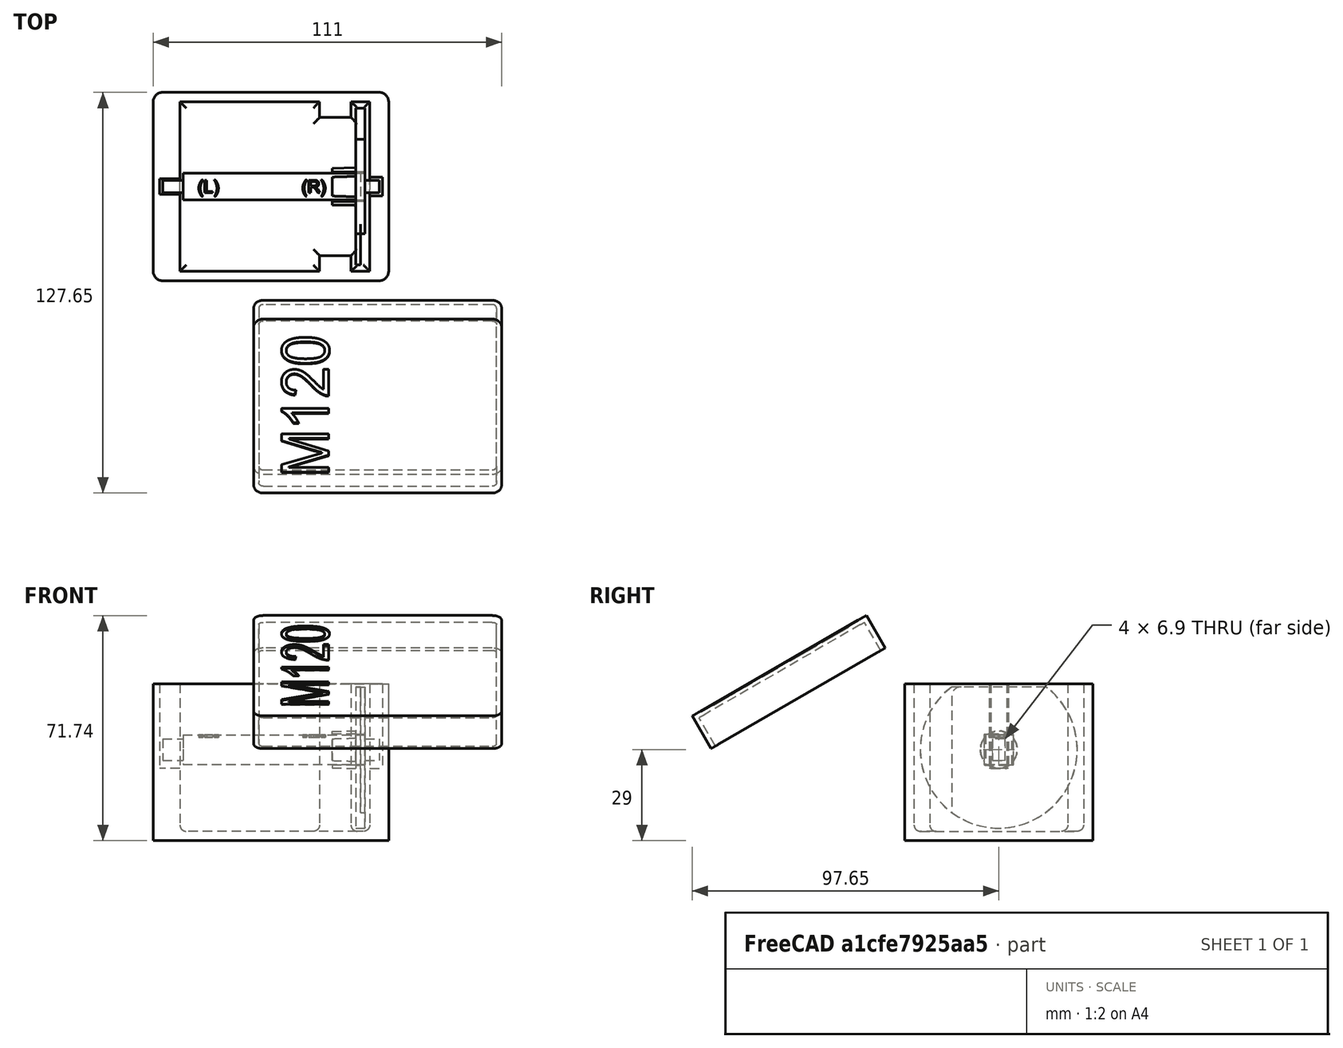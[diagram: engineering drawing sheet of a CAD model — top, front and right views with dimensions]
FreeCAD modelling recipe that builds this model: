
FCSTD DOCUMENT  (FreeCAD 1.0R39109 (Git))
Label: Phomeno_M120_Rolle
License: All rights reserved
LicenseURL: https://en.wikipedia.org/wiki/All_rights_reserved
objects: TechDraw::DrawViewDimension×24, Sketcher::SketchObject×13, PartDesign::Pad×7, PartDesign::Pocket×6, TechDraw::DrawProjGroupItem×6, PartDesign::Body×5, Part::Part2DObjectPython×2, PartDesign::Fillet×2, TechDraw::DrawSVGTemplate×2, TechDraw::DrawProjGroup×2, TechDraw::DrawPage×2, PartDesign::FeatureBase×1, PartDesign::Plane×1, PartDesign::Mirrored×1, PartDesign::Thickness×1, Part::Fuse×1
note: 124 computed .brp shape members not serialized (recipe doc carries the construction recipe); baked Part::Feature solids carry a one-line shape summary decoded from their .brp

FEATURE [Sketcher::SketchObject] Sketch  label="s_Basis_Platte_links"
  ArcFitTolerance = 1e-06
  AttachmentSupport = -> [YZ_Plane]
  FullyConstrained = true
  MakeInternals = false
  MapMode = 5
  Placement = pos=(0,0,0) rot=(0.57735,0.57735,0.57735;2.0944rad)
  sketch-geometry (3):
    g0: Circle [constr] CenterX=0 CenterY=0 CenterZ=0 NormalX=0 NormalY=0 NormalZ=1 AngleXU=0 Radius=25
    g1: LineSegment StartX=-15 StartY=20 StartZ=0 EndX=15 EndY=20 EndZ=0
    g2: ArcOfCircle CenterX=0 CenterY=0 CenterZ=0 NormalX=0 NormalY=0 NormalZ=1 AngleXU=0 Radius=25 StartAngle=2.2143 EndAngle=7.21048
  constraints (8):
    c: Coincident(g0,g-1)
    c: Diameter(g0) = 50
    c: PointOnObject(g1,g0)
    c: Horizontal(g1)
    c: Coincident(g2,g1)
    c: Coincident(g2,g0)
    c: Coincident(g2,g1)
    c: Distance(g-1,g1) = 20
FEATURE [PartDesign::Pad] Pad  label="Basis_Platte_links"
  Direction = (1,0,0)
  Length = 1.5
  Length2 = 10
  Placement = pos=(0,0,0) rot=(1,1,1;2.0944rad)
  Profile = -> Sketch
  ReferenceAxis = -> Sketch [N_Axis]
  Refine = true
  Suppressed = false
  Type = 0
FEATURE [Sketcher::SketchObject] Sketch001  label="s_Achsenloch_links"
  ArcFitTolerance = 1e-06
  AttachmentSupport = -> [YZ_Plane]
  FullyConstrained = true
  MakeInternals = false
  MapMode = 5
  Placement = pos=(0,0,0) rot=(0.57735,0.57735,0.57735;2.0944rad)
  sketch-geometry (4):
    g0: LineSegment StartX=-4.5 StartY=5 StartZ=0 EndX=-4.5 EndY=-5 EndZ=0
    g1: LineSegment StartX=-4.5 StartY=-5 StartZ=0 EndX=4.5 EndY=-5 EndZ=0
    g2: LineSegment StartX=4.5 StartY=-5 StartZ=0 EndX=4.5 EndY=5 EndZ=0
    g3: LineSegment StartX=4.5 StartY=5 StartZ=0 EndX=-4.5 EndY=5 EndZ=0
  constraints (11):
    c: Coincident(g0,g1)
    c: Coincident(g1,g2)
    c: Coincident(g2,g3)
    c: Coincident(g3,g0)
    c: Vertical(g0)
    c: Vertical(g2)
    c: Horizontal(g1)
    c: Horizontal(g3)
    c: Distance(g3,g3) = 9
    c: Symmetric(g2,g0,g-1)
    c: Distance(g2,g2) = 10
FEATURE [Sketcher::SketchObject] Sketch002  label="s_Achse_links"
  ArcFitTolerance = 1e-06
  AttachmentSupport = -> [YZ_Plane]
  FullyConstrained = true
  MakeInternals = false
  MapMode = 5
  Placement = pos=(0,0,0) rot=(0.57735,0.57735,0.57735;2.0944rad)
  sketch-geometry (1):
    g0: Circle CenterX=0 CenterY=0 CenterZ=0 NormalX=0 NormalY=0 NormalZ=1 AngleXU=0 Radius=6
  constraints (2):
    c: Coincident(g0,g-1)
    c: Diameter(g0) = 12
FEATURE [PartDesign::Pad] Pad001  label="Achse_links"
  BaseFeature = -> Pad
  Direction = (1,0,0)
  Length = 9
  Length2 = 10
  Placement = pos=(0,0,0) rot=(1,1,1;2.0944rad)
  Profile = -> Sketch002
  ReferenceAxis = -> Sketch002 [N_Axis]
  Refine = true
  Suppressed = false
  TaperAngle = -1
  Type = 0
FEATURE [PartDesign::Pocket] Pocket  label="Achsenloch_links"
  BaseFeature = -> Pad001
  Direction = (-1,0,0)
  Length = 10
  Length2 = 10
  Midplane = true
  Placement = pos=(0,0,0) rot=(1,1,1;2.0944rad)
  Profile = -> Sketch001
  ReferenceAxis = -> Sketch001 [N_Axis]
  Refine = true
  Suppressed = false
  Type = 1
FEATURE [Sketcher::SketchObject] Sketch003  label="s_Aussparung_Achse_links"
  ArcFitTolerance = 1e-06
  AttachmentSupport = -> [YZ_Plane]
  ExternalGeometry = -> [Sketch001]
  FullyConstrained = true
  MakeInternals = false
  MapMode = 5
  Placement = pos=(0,0,0) rot=(0.57735,0.57735,0.57735;2.0944rad)
  sketch-geometry (4):
    g0: LineSegment StartX=-4.7 StartY=4.8 StartZ=0 EndX=-4.7 EndY=-4.8 EndZ=0
    g1: LineSegment StartX=-4.7 StartY=-4.8 StartZ=0 EndX=4.7 EndY=-4.8 EndZ=0
    g2: LineSegment StartX=4.7 StartY=-4.8 StartZ=0 EndX=4.7 EndY=4.8 EndZ=0
    g3: LineSegment StartX=4.7 StartY=4.8 StartZ=0 EndX=-4.7 EndY=4.8 EndZ=0
  constraints (11):
    c: Coincident(g0,g1)
    c: Coincident(g1,g2)
    c: Coincident(g2,g3)
    c: Coincident(g3,g0)
    c: Vertical(g0)
    c: Vertical(g2)
    c: Horizontal(g1)
    c: Horizontal(g3)
    c: Symmetric(g2,g0,g-1)
    c: Distance(g-3,g3) = 0.2
    c: DistanceX(g-4,g2) = 0.2
FEATURE [PartDesign::Pocket] Pocket001  label="Aussparung_Achse_links"
  BaseFeature = -> Pocket
  Direction = (-1,0,0)
  Length = 5
  Length2 = 5
  Placement = pos=(0,0,0) rot=(1,1,1;2.0944rad)
  Profile = -> Sketch003
  ReferenceAxis = -> Sketch003 [N_Axis]
  Refine = true
  Reversed = true
  Suppressed = false
  Type = 1
FEATURE [PartDesign::Body] Body  label="Platte_Links"
  AllowCompound = false
  Group = -> [Sketch,Pad,Sketch001,Sketch002,Pad001,Pocket,Sketch003,Pocket001]
  Origin = -> Origin
  Placement = pos=(-14,0,0) rot=(0,0,1;0rad)
  Tip = -> Pocket001
FEATURE [Sketcher::SketchObject] Sketch004  label="s_Achse_aussen"
  ArcFitTolerance = 1e-06
  AttachmentSupport = -> [YZ_Plane001]
  FullyConstrained = true
  MakeInternals = false
  MapMode = 5
  Placement = pos=(0,0,0) rot=(0.57735,0.57735,0.57735;2.0944rad)
  sketch-geometry (4):
    g0: LineSegment StartX=-4.25 StartY=4.75 StartZ=0 EndX=-4.25 EndY=-4.75 EndZ=0
    g1: LineSegment StartX=-4.25 StartY=-4.75 StartZ=0 EndX=4.25 EndY=-4.75 EndZ=0
    g2: LineSegment StartX=4.25 StartY=-4.75 StartZ=0 EndX=4.25 EndY=4.75 EndZ=0
    g3: LineSegment StartX=4.25 StartY=4.75 StartZ=0 EndX=-4.25 EndY=4.75 EndZ=0
  constraints (11):
    c: Coincident(g0,g1)
    c: Coincident(g1,g2)
    c: Coincident(g2,g3)
    c: Coincident(g3,g0)
    c: Vertical(g0)
    c: Vertical(g2)
    c: Horizontal(g1)
    c: Horizontal(g3)
    c: Symmetric(g2,g0,g-1)
    c: Distance(g1,g1) = 8.5
    c: Distance(g2,g2) = 9.5
FEATURE [Sketcher::SketchObject] Sketch005  label="s_Achse_innen"
  ArcFitTolerance = 1e-06
  AttachmentSupport = -> [YZ_Plane001]
  FullyConstrained = true
  MakeInternals = false
  MapMode = 5
  Placement = pos=(0,0,0) rot=(0.57735,0.57735,0.57735;2.0944rad)
  sketch-geometry (4):
    g0: LineSegment StartX=-2 StartY=3.45 StartZ=0 EndX=-2 EndY=-3.45 EndZ=0
    g1: LineSegment StartX=-2 StartY=-3.45 StartZ=0 EndX=2 EndY=-3.45 EndZ=0
    g2: LineSegment StartX=2 StartY=-3.45 StartZ=0 EndX=2 EndY=3.45 EndZ=0
    g3: LineSegment StartX=2 StartY=3.45 StartZ=0 EndX=-2 EndY=3.45 EndZ=0
  constraints (11):
    c: Coincident(g0,g1)
    c: Coincident(g1,g2)
    c: Coincident(g2,g3)
    c: Coincident(g3,g0)
    c: Vertical(g0)
    c: Vertical(g2)
    c: Horizontal(g1)
    c: Horizontal(g3)
    c: Symmetric(g2,g0,g-1)
    c: Distance(g3,g3) = 4
    c: DistanceY(g2,g2) = 6.9
FEATURE [PartDesign::Pad] Pad002  label="Achse_innen"
  Direction = (1,0,0)
  Length = 69
  Length2 = 10
  Midplane = true
  Placement = pos=(0,0,0) rot=(1,1,1;2.0944rad)
  Profile = -> Sketch005
  ReferenceAxis = -> Sketch005 [N_Axis]
  Refine = true
  Suppressed = false
  Type = 0
FEATURE [PartDesign::Pad] Pad003  label="Achse_aussen"
  BaseFeature = -> Pad002
  Direction = (1,0,0)
  Length = 30
  Length2 = 28
  Midplane = true
  Placement = pos=(0,0,0) rot=(1,1,1;2.0944rad)
  Profile = -> Sketch004
  ReferenceAxis = -> Sketch004 [N_Axis]
  Refine = true
  Suppressed = false
  Type = 4
FEATURE [PartDesign::FeatureBase] Clone  label="Clone_Platte_Links"
  BaseFeature = -> Body
  Placement = pos=(-49,0,0) rot=(0,0,1;0rad)
  Suppressed = false
FEATURE [Sketcher::SketchObject] Sketch006  label="s_Auftrag"
  ArcFitTolerance = 1e-06
  AttachmentSupport = -> [Clone]
  ExternalGeometry = -> [Clone]
  FullyConstrained = true
  MakeInternals = false
  MapMode = 5
  Placement = pos=(-49,0,0) rot=(0.57735,-0.57735,-0.57735;2.0944rad)
  sketch-geometry (9):
    g0: LineSegment StartX=15 StartY=20 StartZ=0 EndX=-12 EndY=20 EndZ=0
    g1: LineSegment StartX=-15 StartY=17 StartZ=0 EndX=-15 EndY=-20 EndZ=0
    g2: ArcOfCircle CenterX=0 CenterY=0 CenterZ=0 NormalX=0 NormalY=0 NormalZ=1 AngleXU=0 Radius=25 StartAngle=4.06889 EndAngle=7.21048
    g3: LineSegment StartX=-4.7 StartY=4.8 StartZ=0 EndX=-4.7 EndY=-4.8 EndZ=0
    g4: LineSegment StartX=-4.7 StartY=-4.8 StartZ=0 EndX=4.7 EndY=-4.8 EndZ=0
    g5: LineSegment StartX=4.7 StartY=-4.8 StartZ=0 EndX=4.7 EndY=4.8 EndZ=0
    g6: LineSegment StartX=4.7 StartY=4.8 StartZ=0 EndX=-4.7 EndY=4.8 EndZ=0
    g7: ArcOfCircle CenterX=-12 CenterY=17 CenterZ=0 NormalX=0 NormalY=0 NormalZ=1 AngleXU=0 Radius=3 StartAngle=1.5708 EndAngle=3.14159
    g8: GeomPoint [constr] X=-15 Y=20 Z=0
  constraints (21):
    c: Coincident(g0,g-4)
    c: Coincident(g8,g-4)
    c: Coincident(g2,g0)
    c: Coincident(g2,g1)
    c: Coincident(g2,g-1)
    c: Coincident(g3,g4)
    c: Coincident(g4,g5)
    c: Coincident(g5,g6)
    c: Coincident(g6,g3)
    c: Vertical(g3)
    c: Vertical(g5)
    c: Horizontal(g4)
    c: Horizontal(g6)
    c: Coincident(g3,g-6)
    c: Coincident(g4,g-8)
    c: Vertical(g1)
    c: PointOnObject(g8,g0)
    c: PointOnObject(g8,g1)
    c: Tangent(g0,g7) = -1.5708
    c: Tangent(g1,g7) = -1.5708
    c: Radius(g7) = 3
FEATURE [PartDesign::Pad] Pad004  label="Auftrag"
  BaseFeature = -> Clone
  Direction = (-1,0,0)
  Length = 1.5
  Length2 = 10
  Placement = pos=(-49,0,0) rot=(0,0,1;0rad)
  Profile = -> Sketch006
  ReferenceAxis = -> Sketch006 [N_Axis]
  Refine = true
  Suppressed = false
  Type = 0
FEATURE [PartDesign::Body] Body003  label="Platte_Rechts"
  AllowCompound = false
  Group = -> [Clone,Sketch006,Pad004]
  Origin = -> Origin003
  Placement = pos=(-20.5,1.54e-14,0) rot=(0,0,1;3.14159rad)
  Tip = -> Pad004
FEATURE [Part::Part2DObjectPython] ShapeString  label="ss_Beschriftung"  # Draft 2D object (typed FeaturePython)
  FontFile = <path>
  Fuse = false
  Justification = 6
  JustificationReference = 0
  KeepLeftMargin = false
  MakeFace = true
  ObliqueAngle = 0
  Placement = pos=(-23,-2,5) rot=(0,0,1;0rad)
  ScaleToSize = true
  Size = 4
  String = (L)                 (R)
  Tracking = 0
FEATURE [Sketcher::SketchObject] Sketch008  label="s_Box-Body"
  ArcFitTolerance = 1e-06
  AttachmentSupport = -> [XY_Plane004]
  FullyConstrained = true
  MakeInternals = false
  MapMode = 5
  sketch-geometry (4):
    g0: LineSegment StartX=-37.5 StartY=30 StartZ=0 EndX=-37.5 EndY=-30 EndZ=0
    g1: LineSegment StartX=-37.5 StartY=-30 StartZ=0 EndX=37.5 EndY=-30 EndZ=0
    g2: LineSegment StartX=37.5 StartY=-30 StartZ=0 EndX=37.5 EndY=30 EndZ=0
    g3: LineSegment StartX=37.5 StartY=30 StartZ=0 EndX=-37.5 EndY=30 EndZ=0
  constraints (11):
    c: Coincident(g0,g1)
    c: Coincident(g1,g2)
    c: Coincident(g2,g3)
    c: Coincident(g3,g0)
    c: Vertical(g0)
    c: Vertical(g2)
    c: Horizontal(g1)
    c: Horizontal(g3)
    c: Symmetric(g2,g0,g-1)
    c: DistanceX(g1,g1) = 75
    c: DistanceY(g2,g2) = 60
FEATURE [PartDesign::Pad] Pad005  label="Box-Body"
  Direction = (0,0,1)
  Length = 21
  Length2 = 29
  Midplane = true
  Profile = -> Sketch008
  ReferenceAxis = -> Sketch008 [N_Axis]
  Refine = true
  Suppressed = false
  Type = 4
FEATURE [PartDesign::Plane] DatumPlane  label="dp_top"
  AttachmentSupport = -> [Pad005]
  Length = 88.4164
  MapMode = 5
  Placement = pos=(0,0,21) rot=(0,0,1;0rad)
  ResizeMode = 0
  Width = 73.4164
FEATURE [Sketcher::SketchObject] Sketch009  label="s_Box-Innen"
  ArcFitTolerance = 1e-06
  AttachmentSupport = -> [DatumPlane]
  ExternalGeometry = -> [Sketch008]
  FullyConstrained = true
  MakeInternals = false
  MapMode = 5
  Placement = pos=(0,0,21) rot=(0,0,1;0rad)
  sketch-geometry (8):
    g0: LineSegment StartX=31.5 StartY=0 StartZ=0 EndX=31.5 EndY=27 EndZ=0
    g1: LineSegment StartX=31.5 StartY=27 StartZ=0 EndX=25.5 EndY=27 EndZ=0
    g2: LineSegment StartX=25.5 StartY=27 StartZ=0 EndX=25.5 EndY=22 EndZ=0
    g3: LineSegment StartX=-29 StartY=27 StartZ=0 EndX=-29 EndY=0 EndZ=0
    g4: LineSegment StartX=25.5 StartY=22 StartZ=0 EndX=15.5 EndY=22 EndZ=0
    g5: LineSegment StartX=15.5 StartY=22 StartZ=0 EndX=15.5 EndY=27 EndZ=0
    g6: LineSegment StartX=15.5 StartY=27 StartZ=0 EndX=-29 EndY=27 EndZ=0
    g7: LineSegment StartX=-29 StartY=0 StartZ=0 EndX=31.5 EndY=0 EndZ=0
  constraints (24):
    c: Vertical(g0)
    c: Coincident(g0,g1)
    c: Horizontal(g1)
    c: Coincident(g1,g2)
    c: Vertical(g2)
    c: PointOnObject(g0,g-1)
    c: PointOnObject(g3,g-1)
    c: Vertical(g3)
    c: Coincident(g2,g4)
    c: Horizontal(g4)
    c: Coincident(g4,g5)
    c: Vertical(g5)
    c: Coincident(g5,g6)
    c: Horizontal(g6)
    c: Coincident(g3,g6)
    c: DistanceY(g2,g2) = 5
    c: DistanceX(g0,g-4) = 6
    c: DistanceY(g0,g-4) = 3
    c: DistanceX(g1,g1) = 6
    c: DistanceX(g4,g4) = 10
    c: DistanceX(g-5,g3) = 8.5
    c: Equal(g2,g5)
    c: Coincident(g7,g3)
    c: Coincident(g7,g0)
FEATURE [PartDesign::Pocket] Pocket003  label="Box-Innen_halb"
  BaseFeature = -> Pad005
  Direction = (0,0,-1)
  Length = 47
  Length2 = 5
  Profile = -> Sketch009
  ReferenceAxis = -> Sketch009 [N_Axis]
  Refine = true
  Suppressed = false
  Type = 0
FEATURE [PartDesign::Mirrored] Mirrored  label="Box-Innen"
  BaseFeature = -> Pocket003
  MirrorPlane = -> Sketch009 [H_Axis]
  Originals = -> [Pocket003]
  Refine = true
  Suppressed = false
  TransformMode = 0
FEATURE [Sketcher::SketchObject] Sketch010  label="s_Fuehrung_Achse"
  ArcFitTolerance = 1e-06
  AttachmentSupport = -> [DatumPlane]
  ExternalGeometry = -> [Sketch009]
  FullyConstrained = true
  MakeInternals = false
  MapMode = 5
  Placement = pos=(0,0,21) rot=(0,0,1;0rad)
  sketch-geometry (8):
    g0: LineSegment StartX=31.5 StartY=3 StartZ=0 EndX=31.5 EndY=-3 EndZ=0
    g1: LineSegment StartX=31.5 StartY=-3 StartZ=0 EndX=35.5 EndY=-3 EndZ=0
    g2: LineSegment StartX=35.5 StartY=-3 StartZ=0 EndX=35.5 EndY=3 EndZ=0
    g3: LineSegment StartX=35.5 StartY=3 StartZ=0 EndX=31.5 EndY=3 EndZ=0
    g4: LineSegment StartX=-29 StartY=2.5 StartZ=0 EndX=-35.5 EndY=2.5 EndZ=0
    g5: LineSegment StartX=-35.5 StartY=2.5 StartZ=0 EndX=-35.5 EndY=-2.5 EndZ=0
    g6: LineSegment StartX=-35.5 StartY=-2.5 StartZ=0 EndX=-29 EndY=-2.5 EndZ=0
    g7: LineSegment StartX=-29 StartY=-2.5 StartZ=0 EndX=-29 EndY=2.5 EndZ=0
  constraints (22):
    c: Coincident(g0,g1)
    c: Coincident(g1,g2)
    c: Coincident(g2,g3)
    c: Coincident(g3,g0)
    c: Vertical(g0)
    c: Horizontal(g1)
    c: Horizontal(g3)
    c: PointOnObject(g0,g-3)
    c: Symmetric(g2,g1,g-1)
    c: Distance(g3,g3) = 4
    c: DistanceY(g-1,g2) = 3
    c: Coincident(g4,g5)
    c: Coincident(g5,g6)
    c: Coincident(g6,g7)
    c: Coincident(g7,g4)
    c: Horizontal(g4)
    c: Horizontal(g6)
    c: Vertical(g7)
    c: PointOnObject(g4,g-4)
    c: Symmetric(g4,g5,g-1)
    c: DistanceX(g4,g4) = 6.5
    c: DistanceY(g5,g-1) = 2.5
FEATURE [PartDesign::Pocket] Pocket004  label="Fuerhrung_Achse"
  BaseFeature = -> Mirrored
  Direction = (0,0,-1)
  Length = 27
  Length2 = 5
  Profile = -> Sketch010
  ReferenceAxis = -> Sketch010 [N_Axis]
  Refine = true
  Suppressed = false
  Type = 0
FEATURE [PartDesign::Fillet] Fillet  label="Abrundung_Aussenkanten"
  Base = -> Pocket004 [Edge1,Edge5,Edge8,Edge2]
  BaseFeature = -> Pocket004
  Radius = 3
  Refine = true
  SupportTransform = false
  Suppressed = false
  UseAllEdges = false
FEATURE [PartDesign::Fillet] Fillet001  label="Abrundung_innen"
  Base = -> Fillet [Edge77,Edge79,Edge81,Edge83,Edge84,Edge49,Edge57,Edge59,Edge61,Edge63,Edge65,Edge66]
  BaseFeature = -> Fillet
  Radius = 2
  Refine = true
  SupportTransform = false
  Suppressed = false
  UseAllEdges = false
FEATURE [PartDesign::Body] Body004  label="Spool-Box-Body"
  AllowCompound = false
  Group = -> [Sketch008,Pad005,DatumPlane,Sketch009,Pocket003,Mirrored,Sketch010,Pocket004,Fillet,Fillet001]
  Origin = -> Origin004
  Tip = -> Fillet001
FEATURE [Sketcher::SketchObject] Sketch011  label="s_Deckel_Body"
  ArcFitTolerance = 1e-06
  AttachmentSupport = -> [XY_Plane005]
  FullyConstrained = true
  MakeInternals = false
  MapMode = 5
  sketch-geometry (12):
    g0: LineSegment StartX=-39.5 StartY=29 StartZ=0 EndX=-39.5 EndY=-29 EndZ=0
    g1: LineSegment StartX=-36.5 StartY=-32 StartZ=0 EndX=36.5 EndY=-32 EndZ=0
    g2: LineSegment StartX=39.5 StartY=-29 StartZ=0 EndX=39.5 EndY=29 EndZ=0
    g3: LineSegment StartX=36.5 StartY=32 StartZ=0 EndX=-36.5 EndY=32 EndZ=0
    g4: ArcOfCircle CenterX=-36.5 CenterY=29 CenterZ=0 NormalX=0 NormalY=0 NormalZ=1 AngleXU=0 Radius=3 StartAngle=1.5708 EndAngle=3.14159
    g5: GeomPoint [constr] X=-39.5 Y=32 Z=0
    g6: ArcOfCircle CenterX=36.5 CenterY=29 CenterZ=0 NormalX=0 NormalY=0 NormalZ=1 AngleXU=0 Radius=3 StartAngle=4e-16 EndAngle=1.5708
    g7: GeomPoint [constr] X=39.5 Y=32 Z=0
    g8: ArcOfCircle CenterX=36.5 CenterY=-29 CenterZ=0 NormalX=0 NormalY=0 NormalZ=1 AngleXU=0 Radius=3 StartAngle=4.71239 EndAngle=6.28319
    g9: GeomPoint [constr] X=39.5 Y=-32 Z=0
    g10: ArcOfCircle CenterX=-36.5 CenterY=-29 CenterZ=0 NormalX=0 NormalY=0 NormalZ=1 AngleXU=0 Radius=3 StartAngle=3.14159 EndAngle=4.71239
    g11: GeomPoint [constr] X=-39.5 Y=-32 Z=0
  constraints (27):
    c: Vertical(g0)
    c: Vertical(g2)
    c: Horizontal(g1)
    c: Horizontal(g3)
    c: Symmetric(g7,g11,g-1)
    c: DistanceX(g5,g7) = 79
    c: DistanceY(g9,g7) = 64
    c: PointOnObject(g5,g0)
    c: PointOnObject(g5,g3)
    c: Tangent(g0,g4) = -1.5708
    c: Tangent(g3,g4) = -1.5708
    c: PointOnObject(g7,g2)
    c: PointOnObject(g7,g3)
    c: Tangent(g2,g6) = -1.5708
    c: Tangent(g3,g6) = -1.5708
    c: PointOnObject(g9,g1)
    c: PointOnObject(g9,g2)
    c: Tangent(g1,g8) = -1.5708
    c: Tangent(g2,g8) = -1.5708
    c: PointOnObject(g11,g0)
    c: PointOnObject(g11,g1)
    c: Tangent(g0,g10) = -1.5708
    c: Tangent(g1,g10) = -1.5708
    c: Radius(g4) = 3
    c: Equal(g4,g6)
    c: Equal(g6,g8)
    c: Equal(g8,g10)
FEATURE [PartDesign::Pad] Pad006  label="Deckel_Body"
  Direction = (0,0,1)
  Length = 12
  Length2 = 10
  Profile = -> Sketch011
  ReferenceAxis = -> Sketch011 [N_Axis]
  Refine = true
  Suppressed = false
  Type = 0
FEATURE [PartDesign::Thickness] Thickness  label="Deckelform"
  Base = -> Pad006 [Face9]
  BaseFeature = -> Pad006
  Intersection = false
  Join = 0
  Mode = 0
  Refine = true
  Reversed = true
  SupportTransform = false
  Suppressed = false
  Value = 1.6
FEATURE [Part::Part2DObjectPython] ShapeString001  label="ss_Schrift_Deckel"  # Draft 2D object (typed FeaturePython)
  FontFile = <path>
  Fuse = false
  Justification = 6
  JustificationReference = 0
  KeepLeftMargin = false
  MakeFace = true
  ObliqueAngle = 0
  Placement = pos=(-31.53,-9.43,0) rot=(0,0,1;0rad)
  ScaleToSize = true
  Size = 15
  String = M120
  Tracking = 0
FEATURE [Sketcher::SketchObject] Sketch012  label="s_Schrift_Deckel"
  ArcFitTolerance = 1e-06
  AttachmentOffset = pos=(-25,7,0) rot=(0,0,1;1.5708rad)
  AttachmentSupport = -> [Thickness]
  FullyConstrained = false
  MakeInternals = false
  MapMode = 5
  Placement = pos=(-25,7,12) rot=(0,0,1;1.5708rad)
  sketch-geometry (66):
    g0: LineSegment StartX=-31.53 StartY=-9.43 StartZ=0 EndX=-31.53 EndY=5.57 EndZ=0
    g1: LineSegment StartX=-29.6189 StartY=-9.43 StartZ=0 EndX=-31.53 EndY=-9.43 EndZ=0
    g2: LineSegment StartX=-29.6189 StartY=3.34207 StartZ=0 EndX=-29.6189 EndY=-9.43 EndZ=0
    g3: LineSegment StartX=-25.2857 StartY=-9.43 StartZ=0 EndX=-29.6189 EndY=3.34207 EndZ=0
    g4: LineSegment StartX=-23.4972 StartY=-9.43 StartZ=0 EndX=-25.2857 EndY=-9.43 EndZ=0
    g5: LineSegment StartX=-19.1436 StartY=3.12746 StartZ=0 EndX=-23.4972 EndY=-9.43 EndZ=0
    g6: LineSegment StartX=-19.1436 StartY=-9.43 StartZ=0 EndX=-19.1436 EndY=3.12746 EndZ=0
    g7: LineSegment StartX=-17.2324 StartY=-9.43 StartZ=0 EndX=-19.1436 EndY=-9.43 EndZ=0
    g8: LineSegment StartX=-17.2324 StartY=5.57 StartZ=0 EndX=-17.2324 EndY=-9.43 EndZ=0
    g9: LineSegment StartX=-19.8998 StartY=5.57 StartZ=0 EndX=-17.2324 EndY=5.57 EndZ=0
    g10: LineSegment StartX=-23.487 StartY=-4.86854 StartZ=0 EndX=-19.8998 EndY=5.57 EndZ=0
    g11: BSplineCurve PolesCount=3 KnotsCount=2 Degree=2 IsPeriodic=0
    g12: BSplineCurve PolesCount=3 KnotsCount=2 Degree=2 IsPeriodic=0
    g13: LineSegment StartX=-28.5458 StartY=5.57 StartZ=0 EndX=-24.9995 EndY=-5.05318 EndZ=0
    g14: LineSegment StartX=-31.53 StartY=5.57 StartZ=0 EndX=-28.5458 EndY=5.57 EndZ=0
    g15: LineSegment StartX=-7.84382 StartY=-9.43 StartZ=0 EndX=-9.68339 EndY=-9.43 EndZ=0
    g16: LineSegment StartX=-7.84382 StartY=5.65721 StartZ=0 EndX=-7.84382 EndY=-9.43 EndZ=0
    g17: LineSegment StartX=-9.02932 StartY=5.65721 StartZ=0 EndX=-7.84382 EndY=5.65721 EndZ=0
    g18: BSplineCurve PolesCount=3 KnotsCount=2 Degree=2 IsPeriodic=0
    g19: BSplineCurve PolesCount=3 KnotsCount=2 Degree=2 IsPeriodic=0
    g20: LineSegment StartX=-13.3625 StartY=0.119419 StartZ=0 EndX=-13.3625 EndY=1.90721 EndZ=0
    g21: BSplineCurve PolesCount=3 KnotsCount=2 Degree=2 IsPeriodic=0
    g22: BSplineCurve PolesCount=3 KnotsCount=2 Degree=2 IsPeriodic=0
    g23: LineSegment StartX=-9.68339 StartY=-9.43 StartZ=0 EndX=-9.68339 EndY=2.32622 EndZ=0
    g24: LineSegment StartX=6.53754 StartY=-7.69672 StartZ=0 EndX=6.53754 EndY=-9.43 EndZ=0
    g25: LineSegment StartX=-0.810523 StartY=-7.69672 StartZ=0 EndX=6.53754 EndY=-7.69672 EndZ=0
    g26: BSplineCurve PolesCount=3 KnotsCount=2 Degree=2 IsPeriodic=0
    g27: BSplineCurve PolesCount=3 KnotsCount=2 Degree=2 IsPeriodic=0
    g28: BSplineCurve PolesCount=3 KnotsCount=2 Degree=2 IsPeriodic=0
    g29: BSplineCurve PolesCount=3 KnotsCount=2 Degree=2 IsPeriodic=0
    g30: BSplineCurve PolesCount=3 KnotsCount=2 Degree=2 IsPeriodic=0
    g31: BSplineCurve PolesCount=3 KnotsCount=2 Degree=2 IsPeriodic=0
    g32: BSplineCurve PolesCount=3 KnotsCount=2 Degree=2 IsPeriodic=0
    g33: BSplineCurve PolesCount=3 KnotsCount=2 Degree=2 IsPeriodic=0
    g34: BSplineCurve PolesCount=3 KnotsCount=2 Degree=2 IsPeriodic=0
    g35: LineSegment StartX=-1.12734 StartY=1.07872 StartZ=0 EndX=-3.01801 EndY=1.27494 EndZ=0
    g36: BSplineCurve PolesCount=3 KnotsCount=2 Degree=2 IsPeriodic=0
    g37: BSplineCurve PolesCount=3 KnotsCount=2 Degree=2 IsPeriodic=0
    g38: BSplineCurve PolesCount=3 KnotsCount=2 Degree=2 IsPeriodic=0
    g39: BSplineCurve PolesCount=3 KnotsCount=2 Degree=2 IsPeriodic=0
    g40: BSplineCurve PolesCount=3 KnotsCount=2 Degree=2 IsPeriodic=0
    g41: BSplineCurve PolesCount=3 KnotsCount=2 Degree=2 IsPeriodic=0
    g42: BSplineCurve PolesCount=3 KnotsCount=2 Degree=2 IsPeriodic=0
    g43: BSplineCurve PolesCount=3 KnotsCount=2 Degree=2 IsPeriodic=0
    g44: BSplineCurve PolesCount=3 KnotsCount=2 Degree=2 IsPeriodic=0
    g45: LineSegment StartX=6.53754 StartY=-9.43 StartZ=0 EndX=-3.36548 EndY=-9.43 EndZ=0
    g46: BSplineCurve PolesCount=3 KnotsCount=2 Degree=2 IsPeriodic=0
    g47: BSplineCurve PolesCount=3 KnotsCount=2 Degree=2 IsPeriodic=0
    g48: BSplineCurve PolesCount=3 KnotsCount=2 Degree=2 IsPeriodic=0
    g49: BSplineCurve PolesCount=3 KnotsCount=2 Degree=2 IsPeriodic=0
    g50: BSplineCurve PolesCount=3 KnotsCount=2 Degree=2 IsPeriodic=0
    g51: BSplineCurve PolesCount=3 KnotsCount=2 Degree=2 IsPeriodic=0
    g52: BSplineCurve PolesCount=3 KnotsCount=2 Degree=2 IsPeriodic=0
    g53: BSplineCurve PolesCount=3 KnotsCount=2 Degree=2 IsPeriodic=0
    g54: BSplineCurve PolesCount=3 KnotsCount=2 Degree=2 IsPeriodic=0
    g55: BSplineCurve PolesCount=3 KnotsCount=2 Degree=2 IsPeriodic=0
    g56: BSplineCurve PolesCount=3 KnotsCount=2 Degree=2 IsPeriodic=0
    g57: BSplineCurve PolesCount=3 KnotsCount=2 Degree=2 IsPeriodic=0
    g58: BSplineCurve PolesCount=3 KnotsCount=2 Degree=2 IsPeriodic=0
    g59: BSplineCurve PolesCount=3 KnotsCount=2 Degree=2 IsPeriodic=0
    g60: BSplineCurve PolesCount=3 KnotsCount=2 Degree=2 IsPeriodic=0
    g61: BSplineCurve PolesCount=3 KnotsCount=2 Degree=2 IsPeriodic=0
    g62: BSplineCurve PolesCount=3 KnotsCount=2 Degree=2 IsPeriodic=0
    g63: BSplineCurve PolesCount=3 KnotsCount=2 Degree=2 IsPeriodic=0
    g64: BSplineCurve PolesCount=3 KnotsCount=2 Degree=2 IsPeriodic=0
    g65: BSplineCurve PolesCount=3 KnotsCount=2 Degree=2 IsPeriodic=0
  constraints (83):
    c: Vertical(g0)
    c: Coincident(g0,g1)
    c: Horizontal(g1)
    c: Coincident(g1,g2)
    c: Vertical(g2)
    c: Coincident(g2,g3)
    c: Coincident(g3,g4)
    c: Horizontal(g4)
    c: Coincident(g4,g5)
    c: Coincident(g5,g6)
    c: Vertical(g6)
    c: Coincident(g6,g7)
    c: Horizontal(g7)
    c: Coincident(g7,g8)
    c: Vertical(g8)
    c: Coincident(g8,g9)
    c: Horizontal(g9)
    c: Coincident(g9,g10)
    c: Coincident(g10,g11)
    c: Coincident(g11,g12)
    c: Coincident(g12,g13)
    c: Coincident(g13,g14)
    c: Horizontal(g14)
    c: Coincident(g14,g0)
    c: Horizontal(g15)
    c: Coincident(g15,g16)
    c: Vertical(g16)
    c: Coincident(g16,g17)
    c: Horizontal(g17)
    c: Coincident(g17,g18)
    c: Coincident(g18,g19)
    c: Coincident(g19,g20)
    c: Vertical(g20)
    c: Coincident(g20,g21)
    c: Coincident(g21,g22)
    c: Coincident(g22,g23)
    c: Vertical(g23)
    c: Coincident(g23,g15)
    c: Vertical(g24)
    c: Coincident(g24,g25)
    c: Horizontal(g25)
    c: Coincident(g25,g26)
    c: Coincident(g26,g27)
    c: Coincident(g27,g28)
    c: Coincident(g28,g29)
    c: Coincident(g29,g30)
    c: Coincident(g30,g31)
    c: Coincident(g31,g32)
    c: Coincident(g32,g33)
    c: Coincident(g33,g34)
    c: Coincident(g34,g35)
    c: Coincident(g35,g36)
    c: Coincident(g36,g37)
    c: Coincident(g37,g38)
    c: Coincident(g38,g39)
    c: Coincident(g39,g40)
    c: Coincident(g40,g41)
    c: Coincident(g41,g42)
    c: Coincident(g42,g43)
    c: Coincident(g43,g44)
    c: Coincident(g44,g45)
    c: Horizontal(g45)
    c: Coincident(g45,g24)
    c: Coincident(g46,g47)
    c: Coincident(g47,g48)
    c: Coincident(g48,g49)
    c: Coincident(g49,g50)
    c: Coincident(g50,g51)
    c: Coincident(g51,g52)
    c: Coincident(g52,g53)
    c: Coincident(g53,g54)
    c: Coincident(g54,g55)
    c: Coincident(g55,g56)
    c: Coincident(g56,g57)
    c: Coincident(g57,g46)
    c: Coincident(g58,g59)
    c: Coincident(g59,g60)
    c: Coincident(g60,g61)
    c: Coincident(g61,g62)
    c: Coincident(g62,g63)
    c: Coincident(g63,g64)
    c: Coincident(g64,g65)
    c: Coincident(g65,g58)
FEATURE [PartDesign::Pocket] Pocket005  label="SchriftDeckel"
  BaseFeature = -> Thickness
  Direction = (0,0,-1)
  Length = 0.4
  Length2 = 5
  Profile = -> Sketch012
  ReferenceAxis = -> Sketch012 [N_Axis]
  Refine = true
  Suppressed = false
  Type = 0
FEATURE [PartDesign::Body] Body005  label="Spool-Box-Deckel"
  AllowCompound = false
  Group = -> [Sketch011,Pad006,Thickness,ShapeString001,Sketch012,Pocket005]
  Origin = -> Origin005
  Placement = pos=(34,-63.9379,16.3507) rot=(1,0,0;0.523599rad)
  Tip = -> Pocket005
FEATURE [Sketcher::SketchObject] Sketch013  label="s_Beschriftung"
  ArcFitTolerance = 1e-06
  FullyConstrained = false
  MakeInternals = false
  Placement = pos=(0,0,5) rot=(0,0,1;0rad)
  sketch-geometry (73):
    g0: BSplineCurve PolesCount=3 KnotsCount=2 Degree=2 IsPeriodic=0
    g1: LineSegment StartX=-21.681 StartY=-3.16279 StartZ=0 EndX=-22.0325 EndY=-3.16279 EndZ=0
    g2: BSplineCurve PolesCount=3 KnotsCount=2 Degree=2 IsPeriodic=0
    g3: BSplineCurve PolesCount=3 KnotsCount=2 Degree=2 IsPeriodic=0
    g4: BSplineCurve PolesCount=3 KnotsCount=2 Degree=2 IsPeriodic=0
    g5: BSplineCurve PolesCount=3 KnotsCount=2 Degree=2 IsPeriodic=0
    g6: LineSegment StartX=-22.0325 StartY=2.06977 StartZ=0 EndX=-21.681 EndY=2.06977 EndZ=0
    g7: BSplineCurve PolesCount=3 KnotsCount=2 Degree=2 IsPeriodic=0
    g8: BSplineCurve PolesCount=3 KnotsCount=2 Degree=2 IsPeriodic=0
    g9: BSplineCurve PolesCount=3 KnotsCount=2 Degree=2 IsPeriodic=0
    g10: LineSegment StartX=-21.0687 StartY=-2 StartZ=0 EndX=-21.0687 EndY=2 EndZ=0
    g11: LineSegment StartX=-18.5723 StartY=-2 StartZ=0 EndX=-21.0687 EndY=-2 EndZ=0
    g12: LineSegment StartX=-18.5723 StartY=-1.53779 StartZ=0 EndX=-18.5723 EndY=-2 EndZ=0
    g13: LineSegment StartX=-20.54 StartY=-1.53779 StartZ=0 EndX=-18.5723 EndY=-1.53779 EndZ=0
    g14: LineSegment StartX=-20.54 StartY=2 StartZ=0 EndX=-20.54 EndY=-1.53779 EndZ=0
    g15: LineSegment StartX=-21.0687 StartY=2 StartZ=0 EndX=-20.54 EndY=2 EndZ=0
    g16: LineSegment StartX=-17.6833 StartY=-3.16279 StartZ=0 EndX=-18.0349 EndY=-3.16279 EndZ=0
    g17: BSplineCurve PolesCount=3 KnotsCount=2 Degree=2 IsPeriodic=0
    g18: BSplineCurve PolesCount=3 KnotsCount=2 Degree=2 IsPeriodic=0
    g19: BSplineCurve PolesCount=3 KnotsCount=2 Degree=2 IsPeriodic=0
    g20: BSplineCurve PolesCount=3 KnotsCount=2 Degree=2 IsPeriodic=0
    g21: LineSegment StartX=-18.0349 StartY=2.06977 StartZ=0 EndX=-17.6833 EndY=2.06977 EndZ=0
    g22: BSplineCurve PolesCount=3 KnotsCount=2 Degree=2 IsPeriodic=0
    g23: BSplineCurve PolesCount=3 KnotsCount=2 Degree=2 IsPeriodic=0
    g24: BSplineCurve PolesCount=3 KnotsCount=2 Degree=2 IsPeriodic=0
    g25: BSplineCurve PolesCount=3 KnotsCount=2 Degree=2 IsPeriodic=0
    g26: BSplineCurve PolesCount=3 KnotsCount=2 Degree=2 IsPeriodic=0
    g27: LineSegment StartX=11.4353 StartY=-3.16279 StartZ=0 EndX=11.0838 EndY=-3.16279 EndZ=0
    g28: BSplineCurve PolesCount=3 KnotsCount=2 Degree=2 IsPeriodic=0
    g29: BSplineCurve PolesCount=3 KnotsCount=2 Degree=2 IsPeriodic=0
    g30: BSplineCurve PolesCount=3 KnotsCount=2 Degree=2 IsPeriodic=0
    g31: BSplineCurve PolesCount=3 KnotsCount=2 Degree=2 IsPeriodic=0
    g32: LineSegment StartX=11.0838 StartY=2.06977 StartZ=0 EndX=11.4353 EndY=2.06977 EndZ=0
    g33: BSplineCurve PolesCount=3 KnotsCount=2 Degree=2 IsPeriodic=0
    g34: BSplineCurve PolesCount=3 KnotsCount=2 Degree=2 IsPeriodic=0
    g35: BSplineCurve PolesCount=3 KnotsCount=2 Degree=2 IsPeriodic=0
    g36: LineSegment StartX=12.0776 StartY=-2 StartZ=0 EndX=12.0776 EndY=2 EndZ=0
    g37: LineSegment StartX=12.6063 StartY=-2 StartZ=0 EndX=12.0776 EndY=-2 EndZ=0
    g38: LineSegment StartX=12.6063 StartY=-0.218023 StartZ=0 EndX=12.6063 EndY=-2 EndZ=0
    g39: LineSegment StartX=13.2195 StartY=-0.218023 StartZ=0 EndX=12.6063 EndY=-0.218023 EndZ=0
    g40: BSplineCurve PolesCount=3 KnotsCount=2 Degree=2 IsPeriodic=0
    g41: BSplineCurve PolesCount=3 KnotsCount=2 Degree=2 IsPeriodic=0
    g42: BSplineCurve PolesCount=3 KnotsCount=2 Degree=2 IsPeriodic=0
    g43: BSplineCurve PolesCount=3 KnotsCount=2 Degree=2 IsPeriodic=0
    g44: LineSegment StartX=14.9337 StartY=-2 StartZ=0 EndX=14.405 EndY=-1.16515 EndZ=0
    g45: LineSegment StartX=15.5987 StartY=-2 StartZ=0 EndX=14.9337 EndY=-2 EndZ=0
    g46: LineSegment StartX=14.9037 StartY=-0.90843 StartZ=0 EndX=15.5987 EndY=-2 EndZ=0
    g47: BSplineCurve PolesCount=3 KnotsCount=2 Degree=2 IsPeriodic=0
    g48: BSplineCurve PolesCount=3 KnotsCount=2 Degree=2 IsPeriodic=0
    g49: BSplineCurve PolesCount=3 KnotsCount=2 Degree=2 IsPeriodic=0
    g50: BSplineCurve PolesCount=3 KnotsCount=2 Degree=2 IsPeriodic=0
    g51: BSplineCurve PolesCount=3 KnotsCount=2 Degree=2 IsPeriodic=0
    g52: BSplineCurve PolesCount=3 KnotsCount=2 Degree=2 IsPeriodic=0
    g53: BSplineCurve PolesCount=3 KnotsCount=2 Degree=2 IsPeriodic=0
    g54: LineSegment StartX=12.0776 StartY=2 StartZ=0 EndX=13.849 EndY=2 EndZ=0
    g55: LineSegment StartX=12.6063 StartY=0.232558 StartZ=0 EndX=13.7427 EndY=0.232558 EndZ=0
    g56: LineSegment StartX=12.6063 StartY=1.54942 StartZ=0 EndX=12.6063 EndY=0.232558 EndZ=0
    g57: LineSegment StartX=13.8708 StartY=1.54942 StartZ=0 EndX=12.6063 EndY=1.54942 EndZ=0
    g58: BSplineCurve PolesCount=3 KnotsCount=2 Degree=2 IsPeriodic=0
    g59: BSplineCurve PolesCount=3 KnotsCount=2 Degree=2 IsPeriodic=0
    g60: BSplineCurve PolesCount=3 KnotsCount=2 Degree=2 IsPeriodic=0
    g61: BSplineCurve PolesCount=3 KnotsCount=2 Degree=2 IsPeriodic=0
    g62: BSplineCurve PolesCount=3 KnotsCount=2 Degree=2 IsPeriodic=0
    g63: LineSegment StartX=16.3632 StartY=-3.16279 StartZ=0 EndX=16.0116 EndY=-3.16279 EndZ=0
    g64: BSplineCurve PolesCount=3 KnotsCount=2 Degree=2 IsPeriodic=0
    g65: BSplineCurve PolesCount=3 KnotsCount=2 Degree=2 IsPeriodic=0
    g66: BSplineCurve PolesCount=3 KnotsCount=2 Degree=2 IsPeriodic=0
    g67: BSplineCurve PolesCount=3 KnotsCount=2 Degree=2 IsPeriodic=0
    g68: LineSegment StartX=16.0116 StartY=2.06977 StartZ=0 EndX=16.3632 EndY=2.06977 EndZ=0
    g69: BSplineCurve PolesCount=3 KnotsCount=2 Degree=2 IsPeriodic=0
    g70: BSplineCurve PolesCount=3 KnotsCount=2 Degree=2 IsPeriodic=0
    g71: BSplineCurve PolesCount=3 KnotsCount=2 Degree=2 IsPeriodic=0
    g72: BSplineCurve PolesCount=3 KnotsCount=2 Degree=2 IsPeriodic=0
  constraints (96):
    c: Coincident(g0,g1)
    c: Horizontal(g1)
    c: Coincident(g1,g2)
    c: Coincident(g2,g3)
    c: Coincident(g3,g4)
    c: Coincident(g4,g5)
    c: Coincident(g5,g6)
    c: Horizontal(g6)
    c: Coincident(g6,g7)
    c: Coincident(g7,g8)
    c: Coincident(g8,g9)
    c: Coincident(g9,g0)
    c: Vertical(g10)
    c: Coincident(g10,g11)
    c: Horizontal(g11)
    c: Coincident(g11,g12)
    c: Vertical(g12)
    c: Coincident(g12,g13)
    c: Horizontal(g13)
    c: Coincident(g13,g14)
    c: Vertical(g14)
    c: Coincident(g14,g15)
    c: Horizontal(g15)
    c: Coincident(g15,g10)
    c: Horizontal(g16)
    c: Coincident(g16,g17)
    c: Coincident(g17,g18)
    c: Coincident(g18,g19)
    c: Coincident(g19,g20)
    c: Coincident(g20,g21)
    c: Horizontal(g21)
    c: Coincident(g21,g22)
    c: Coincident(g22,g23)
    c: Coincident(g23,g24)
    c: Coincident(g24,g25)
    c: Coincident(g25,g16)
    c: Coincident(g26,g27)
    c: Horizontal(g27)
    c: Coincident(g27,g28)
    c: Coincident(g28,g29)
    c: Coincident(g29,g30)
    c: Coincident(g30,g31)
    c: Coincident(g31,g32)
    c: Horizontal(g32)
    c: Coincident(g32,g33)
    c: Coincident(g33,g34)
    c: Coincident(g34,g35)
    c: Coincident(g35,g26)
    c: Vertical(g36)
    c: Coincident(g36,g37)
    c: Horizontal(g37)
    c: Coincident(g37,g38)
    c: Vertical(g38)
    c: Coincident(g38,g39)
    c: Horizontal(g39)
    c: Coincident(g39,g40)
    c: Coincident(g40,g41)
    c: Coincident(g41,g42)
    c: Coincident(g42,g43)
    c: Coincident(g43,g44)
    c: Coincident(g44,g45)
    c: Horizontal(g45)
    c: Coincident(g45,g46)
    c: Coincident(g46,g47)
    c: Coincident(g47,g48)
    c: Coincident(g48,g49)
    c: Coincident(g49,g50)
    c: Coincident(g50,g51)
    c: Coincident(g51,g52)
    c: Coincident(g52,g53)
    c: Coincident(g53,g54)
    c: Horizontal(g54)
    c: Coincident(g54,g36)
    c: Horizontal(g55)
    c: Coincident(g55,g56)
    c: Vertical(g56)
    c: Coincident(g56,g57)
    c: Horizontal(g57)
    c: Coincident(g57,g58)
    c: Coincident(g58,g59)
    c: Coincident(g59,g60)
    c: Coincident(g60,g61)
    c: Coincident(g61,g62)
    c: Coincident(g62,g55)
    c: Horizontal(g63)
    c: Coincident(g63,g64)
    c: Coincident(g64,g65)
    c: Coincident(g65,g66)
    c: Coincident(g66,g67)
    c: Coincident(g67,g68)
    c: Horizontal(g68)
    c: Coincident(g68,g69)
    c: Coincident(g69,g70)
    c: Coincident(g70,g71)
    c: Coincident(g71,g72)
    c: Coincident(g72,g63)
FEATURE [PartDesign::Pocket] Pocket002  label="Beschriftung"
  BaseFeature = -> Pad003
  Direction = (0,0,-1)
  Length = 1
  Length2 = 5
  Placement = pos=(0,0,0) rot=(1,1,1;2.0944rad)
  Profile = -> Sketch013
  Refine = true
  Suppressed = false
  Type = 0
FEATURE [PartDesign::Body] Body001  label="Achse"
  AllowCompound = false
  Group = -> [Sketch004,Sketch005,Pad002,Pad003,ShapeString,Pocket002,Sketch013]
  Origin = -> Origin001
  Tip = -> Pocket002
FEATURE [Part::Fuse] Fusion  label="Achse_mit_Rolle"
  Base = -> Body001
  Tool = -> Body003
FEATURE [TechDraw::DrawSVGTemplate] Template001  label="Vorlage001"
  EditableTexts = creator=Mervyn <owner>; date_of_issue=02.01.2026; document_type=Assembly Drawing; identification_number=DN; language_code=EN; part_material=PLA; revision_index=AAA; sheet_number=2 / 2; sheet_scale=1 : 2; title=Phomeno M120 Rolle Rechts
  Height = 210
  Orientation = 1
  Template = C:/Program Files/FreeCAD 1.0/data/Mod/TechDraw/Templates/A4_Landscape_ISO5457_minimal.svg
  Width = 297
FEATURE [TechDraw::DrawProjGroupItem] View  label="Front"
  CoarseView = false
  Direction = (1,-1e-16,0)
  Focus = 100
  HardHidden = false
  IsoCount = 0
  IsoHidden = false
  IsoVisible = false
  LockPosition = true
  Perspective = false
  Rotation = 0
  RotationVector = (1,0,0)
  Scale = 2
  ScaleType = 2
  ScrubCount = 1
  SeamHidden = false
  SeamVisible = false
  SmoothHidden = false
  SmoothVisible = true
  Source = -> [Body003]
  Type = 0
  X = 0
  XDirection = (1e-16,1,0)
  Y = 0
FEATURE [TechDraw::DrawProjGroupItem] ProjItem  label="Links"
  CoarseView = false
  Direction = (0,-1,0)
  Focus = 100
  HardHidden = false
  IsoCount = 0
  IsoHidden = false
  IsoVisible = false
  LockPosition = false
  Perspective = false
  Rotation = 0
  RotationVector = (1,0,0)
  Scale = 2
  ScaleType = 0
  ScrubCount = 1
  SeamHidden = false
  SeamVisible = false
  SmoothHidden = false
  SmoothVisible = true
  Source = -> [Body003]
  Type = 1
  X = 75.5
  XDirection = (1,0,0)
  Y = 0
FEATURE [TechDraw::DrawProjGroupItem] ProjItem001  label="Rechts"
  CoarseView = false
  Direction = (2e-16,1,0)
  Focus = 100
  HardHidden = false
  IsoCount = 0
  IsoHidden = false
  IsoVisible = false
  LockPosition = false
  Perspective = false
  Rotation = 0
  RotationVector = (1,0,0)
  Scale = 2
  ScaleType = 0
  ScrubCount = 1
  SeamHidden = false
  SeamVisible = false
  SmoothHidden = false
  SmoothVisible = true
  Source = -> [Body003]
  Type = 2
  X = -75.5
  XDirection = (-1,2e-16,0)
  Y = 0
FEATURE [TechDraw::DrawProjGroup] ProjGroup
  Anchor = -> View
  AutoDistribute = true
  LockPosition = false
  ProjectionType = 0
  Rotation = 0
  Scale = 2
  ScaleType = 2
  Source = -> [Body003]
  Views = -> [View,ProjItem,ProjItem001]
  X = 157.559
  Y = 126.515
  spacingX = 15
  spacingY = 15
FEATURE [TechDraw::DrawViewDimension] Dimension  label="Maß"
  AngleOverride = false
  Arbitrary = false
  ArbitraryTolerances = false
  BoxCorners = (2) [(-10.5,-45,-1e-07),(10.5,45,1e-07)]
  EqualTolerance = true
  ExtensionAngle = 0
  FormatSpec = %.2w
  FormatSpecOverTolerance = %+.2w
  FormatSpecUnderTolerance = %+.2w
  Inverted = false
  LineAngle = 0
  LockPosition = false
  MeasureType = 1
  OverTolerance = 0
  References2D = -> [ProjItem]
  Rotation = 0
  ScaleType = 0
  TheoreticalExact = false
  Type = 0
  UnderTolerance = 0
  X = 24.8512
  Y = 54.0086
FEATURE [TechDraw::DrawViewDimension] Dimension001  label="Maß001"
  AngleOverride = false
  Arbitrary = false
  ArbitraryTolerances = false
  BoxCorners = (2) [(-10.5,-45,-1e-07),(10.5,45,1e-07)]
  EqualTolerance = true
  ExtensionAngle = 0
  FormatSpec = %.2w
  FormatSpecOverTolerance = %+.2w
  FormatSpecUnderTolerance = %+.2w
  Inverted = false
  LineAngle = 0
  LockPosition = false
  MeasureType = 1
  OverTolerance = 0
  References2D = -> [ProjItem]
  Rotation = 0
  ScaleType = 0
  TheoreticalExact = false
  Type = 0
  UnderTolerance = 0
  X = 29.6821
  Y = 64.869
FEATURE [TechDraw::DrawViewDimension] Dimension002  label="Maß002"
  AngleOverride = false
  Arbitrary = false
  ArbitraryTolerances = false
  BoxCorners = (2) [(-10.5,-45,-1e-07),(10.5,45,1e-07)]
  EqualTolerance = true
  ExtensionAngle = 0
  FormatSpec = %.2w
  FormatSpecOverTolerance = %+.2w
  FormatSpecUnderTolerance = %+.2w
  Inverted = false
  LineAngle = 0
  LockPosition = false
  MeasureType = 1
  OverTolerance = 0
  References2D = -> [ProjItem001]
  Rotation = 0
  ScaleType = 0
  TheoreticalExact = false
  Type = 0
  UnderTolerance = 0
  X = -34.8113
  Y = 0.051609
FEATURE [TechDraw::DrawViewDimension] Dimension003  label="Maß003"
  AngleOverride = false
  Arbitrary = false
  ArbitraryTolerances = false
  BoxCorners = (2) [(-10.5,-45,-1e-07),(10.5,45,1e-07)]
  EqualTolerance = true
  ExtensionAngle = 0
  FormatSpec = %.2w
  FormatSpecOverTolerance = %+.2w
  FormatSpecUnderTolerance = %+.2w
  Inverted = false
  LineAngle = 0
  LockPosition = false
  MeasureType = 1
  OverTolerance = 0
  References2D = -> [ProjItem001]
  Rotation = 0
  ScaleType = 0
  TheoreticalExact = false
  Type = 0
  UnderTolerance = 0
  X = 18.3575
  Y = 58.6411
FEATURE [TechDraw::DrawViewDimension] Dimension004  label="Maß004"
  AngleOverride = false
  Arbitrary = false
  ArbitraryTolerances = false
  BoxCorners = (2) [(-10.5,-45,-1e-07),(10.5,45,1e-07)]
  EqualTolerance = true
  ExtensionAngle = 0
  FormatSpec = %.2w
  FormatSpecOverTolerance = %+.2w
  FormatSpecUnderTolerance = %+.2w
  Inverted = false
  LineAngle = 0
  LockPosition = false
  MeasureType = 1
  OverTolerance = 0
  References2D = -> [ProjItem001]
  Rotation = 0
  ScaleType = 0
  TheoreticalExact = false
  Type = 2
  UnderTolerance = 0
  X = -42.3568
  Y = -12.2336
FEATURE [TechDraw::DrawViewDimension] Dimension005  label="Maß005"
  AngleOverride = false
  Arbitrary = false
  ArbitraryTolerances = false
  BoxCorners = (2) [(-10.5,-45,-1e-07),(10.5,45,1e-07)]
  EqualTolerance = true
  ExtensionAngle = 0
  FormatSpec = %.2w
  FormatSpecOverTolerance = %+.2w
  FormatSpecUnderTolerance = %+.2w
  Inverted = false
  LineAngle = 0
  LockPosition = false
  MeasureType = 1
  OverTolerance = 0
  References2D = -> [ProjItem001]
  Rotation = 0
  ScaleType = 0
  TheoreticalExact = false
  Type = 0
  UnderTolerance = 0
  X = -21.1731
  Y = -9.85641
FEATURE [TechDraw::DrawViewDimension] Dimension006  label="Maß006"
  AngleOverride = false
  Arbitrary = false
  ArbitraryTolerances = false
  BoxCorners = (2) [(-50,-45,0),(50,45,0)]
  EqualTolerance = true
  ExtensionAngle = 0
  FormatSpec = %.2w
  FormatSpecOverTolerance = %+.2w
  FormatSpecUnderTolerance = %+.2w
  Inverted = false
  LineAngle = 0
  LockPosition = false
  MeasureType = 1
  OverTolerance = 0
  References2D = -> [View]
  Rotation = 0
  ScaleType = 0
  TheoreticalExact = false
  Type = 0
  UnderTolerance = 0
  X = 18.5915
  Y = 28.6433
FEATURE [TechDraw::DrawViewDimension] Dimension007  label="Maß007"
  AngleOverride = false
  Arbitrary = false
  ArbitraryTolerances = false
  BoxCorners = (2) [(-50,-45,0),(50,45,0)]
  EqualTolerance = true
  ExtensionAngle = 0
  FormatSpec = %.2w
  FormatSpecOverTolerance = %+.2w
  FormatSpecUnderTolerance = %+.2w
  Inverted = false
  LineAngle = 0
  LockPosition = false
  MeasureType = 1
  OverTolerance = 0
  References2D = -> [View]
  Rotation = 0
  ScaleType = 0
  TheoreticalExact = false
  Type = 0
  UnderTolerance = 0
  X = 27.8834
  Y = 25.52
FEATURE [TechDraw::DrawViewDimension] Dimension008  label="Maß008"
  AngleOverride = false
  Arbitrary = false
  ArbitraryTolerances = false
  BoxCorners = (2) [(-50,-45,0),(50,45,0)]
  EqualTolerance = true
  ExtensionAngle = 0
  FormatSpec = %.2w
  FormatSpecOverTolerance = %+.2w
  FormatSpecUnderTolerance = %+.2w
  Inverted = false
  LineAngle = 0
  LockPosition = false
  MeasureType = 1
  OverTolerance = 0
  References2D = -> [View]
  Rotation = 0
  ScaleType = 0
  TheoreticalExact = false
  Type = 0
  UnderTolerance = 0
  X = 33.6774
  Y = 59.1041
FEATURE [TechDraw::DrawViewDimension] Dimension009  label="Maß009"
  AngleOverride = false
  Arbitrary = false
  ArbitraryTolerances = false
  BoxCorners = (2) [(-50,-45,0),(50,45,0)]
  EqualTolerance = true
  ExtensionAngle = 0
  FormatSpec = %.2w
  FormatSpecOverTolerance = %+.2w
  FormatSpecUnderTolerance = %+.2w
  Inverted = false
  LineAngle = 0
  LockPosition = false
  MeasureType = 1
  OverTolerance = 0
  References2D = -> [View]
  Rotation = 0
  ScaleType = 0
  TheoreticalExact = false
  Type = 0
  UnderTolerance = 0
  X = 47.2656
  Y = 55.1316
FEATURE [TechDraw::DrawViewDimension] Dimension010  label="Maß010"
  AngleOverride = false
  Arbitrary = false
  ArbitraryTolerances = false
  BoxCorners = (2) [(-50,-45,0),(50,45,0)]
  EqualTolerance = true
  ExtensionAngle = 0
  FormatSpec = R%.2w
  FormatSpecOverTolerance = %+.2w
  FormatSpecUnderTolerance = %+.2w
  Inverted = false
  LineAngle = 0
  LockPosition = false
  MeasureType = 1
  OverTolerance = 0
  References2D = -> [View]
  Rotation = 0
  ScaleType = 0
  TheoreticalExact = false
  Type = 4
  UnderTolerance = 0
  X = 46.3847
  Y = -47.0626
FEATURE [TechDraw::DrawViewDimension] Dimension011  label="Maß011"
  AngleOverride = false
  Arbitrary = false
  ArbitraryTolerances = false
  BoxCorners = (2) [(-10.5,-45,-1e-07),(10.5,45,1e-07)]
  EqualTolerance = true
  ExtensionAngle = 0
  FormatSpec = %.2w
  FormatSpecOverTolerance = %+.2w
  FormatSpecUnderTolerance = %+.2w
  Inverted = false
  LineAngle = 0
  LockPosition = false
  MeasureType = 1
  OverTolerance = 0
  References2D = -> [ProjItem001]
  Rotation = 0
  ScaleType = 0
  TheoreticalExact = false
  Type = 0
  UnderTolerance = 0
  X = 20.1575
  Y = -10.4226
FEATURE [TechDraw::DrawViewDimension] Dimension012  label="Maß012"
  AngleOverride = false
  Arbitrary = false
  ArbitraryTolerances = false
  BoxCorners = (2) [(-50,-45,0),(50,45,0)]
  EqualTolerance = true
  ExtensionAngle = 0
  FormatSpec = R%.2w
  FormatSpecOverTolerance = %+.2w
  FormatSpecUnderTolerance = %+.2w
  Inverted = false
  LineAngle = 0
  LockPosition = false
  MeasureType = 1
  OverTolerance = 0
  References2D = -> [View]
  Rotation = 0
  ScaleType = 0
  TheoreticalExact = false
  Type = 4
  UnderTolerance = 0
  X = -12.9649
  Y = 34.1925
FEATURE [TechDraw::DrawViewDimension] Dimension013  label="Maß013"
  AngleOverride = false
  Arbitrary = false
  ArbitraryTolerances = false
  BoxCorners = (2) [(-50,-45,0),(50,45,0)]
  EqualTolerance = true
  ExtensionAngle = 0
  FormatSpec = %.2w
  FormatSpecOverTolerance = %+.2w
  FormatSpecUnderTolerance = %+.2w
  Inverted = false
  LineAngle = 0
  LockPosition = false
  MeasureType = 1
  OverTolerance = 0
  References2D = -> [View]
  Rotation = 0
  ScaleType = 0
  TheoreticalExact = false
  Type = 2
  UnderTolerance = 0
  X = -41.5735
  Y = 2
FEATURE [TechDraw::DrawPage] Page001  label="TD Disc Right"
  KeepUpdated = true
  NextBalloonIndex = 1
  ProjectionType = 0
  Template = -> Template001
  Views = -> [ProjGroup,Dimension,Dimension001,Dimension002,Dimension003,Dimension004,Dimension005,Dimension006,Dimension007,Dimension008,Dimension009,Dimension010,Dimension011,Dimension012,Dimension013]
FEATURE [TechDraw::DrawSVGTemplate] Template  label="Vorlage"
  EditableTexts = creator=Mervyn <owner>; date_of_issue=02.01.2026; identification_number=DN; language_code=EN; part_material=PLA; revision_index=AAA; sheet_number=1 / 2; sheet_scale=1 : 2; title=Phomeno M120 Axis
  Height = 210
  Orientation = 1
  Template = C:/Program Files/FreeCAD 1.0/data/Mod/TechDraw/Templates/A4_Landscape_ISO5457_minimal.svg
  Width = 297
FEATURE [TechDraw::DrawProjGroupItem] View001  label="Front_1"
  CoarseView = false
  Direction = (0,-1,0)
  Focus = 100
  HardHidden = false
  IsoCount = 0
  IsoHidden = false
  IsoVisible = false
  LockPosition = true
  Perspective = false
  Rotation = 0
  RotationVector = (1,0,0)
  Scale = 2
  ScaleType = 2
  ScrubCount = 1
  SeamHidden = false
  SeamVisible = false
  SmoothHidden = false
  SmoothVisible = true
  Source = -> [Body001]
  Type = 0
  X = 0
  XDirection = (1,0,0)
  Y = 0
FEATURE [TechDraw::DrawProjGroupItem] ProjItem002  label="Links_1"
  CoarseView = false
  Direction = (-1,-1e-16,0)
  Focus = 100
  HardHidden = false
  IsoCount = 0
  IsoHidden = false
  IsoVisible = false
  LockPosition = false
  Perspective = false
  Rotation = 0
  RotationVector = (1,0,0)
  Scale = 2
  ScaleType = 0
  ScrubCount = 1
  SeamHidden = false
  SeamVisible = false
  SmoothHidden = false
  SmoothVisible = true
  Source = -> [Body001]
  Type = 1
  X = 92.5
  XDirection = (1e-16,-1,0)
  Y = 0
FEATURE [TechDraw::DrawProjGroupItem] ProjItem003  label="Rechts_1"
  CoarseView = false
  Direction = (1,-1e-16,0)
  Focus = 100
  HardHidden = false
  IsoCount = 0
  IsoHidden = false
  IsoVisible = false
  LockPosition = false
  Perspective = false
  Rotation = 0
  RotationVector = (1,0,0)
  Scale = 2
  ScaleType = 0
  ScrubCount = 1
  SeamHidden = false
  SeamVisible = false
  SmoothHidden = false
  SmoothVisible = true
  Source = -> [Body001]
  Type = 2
  X = -92.5
  XDirection = (1e-16,1,0)
  Y = 0
FEATURE [TechDraw::DrawProjGroup] ProjGroup001
  Anchor = -> View001
  AutoDistribute = true
  LockPosition = false
  ProjectionType = 0
  Rotation = 0
  Scale = 2
  ScaleType = 2
  Source = -> [Body001]
  Views = -> [View001,ProjItem002,ProjItem003]
  X = 148.5
  Y = 105
  spacingX = 15
  spacingY = 15
FEATURE [TechDraw::DrawViewDimension] Dimension014  label="Maß014"
  AngleOverride = false
  Arbitrary = false
  ArbitraryTolerances = false
  BoxCorners = (2) [(-69,-9.5,0),(69,9.5,0)]
  EqualTolerance = true
  ExtensionAngle = 0
  FormatSpec = %.2w
  FormatSpecOverTolerance = %+.2w
  FormatSpecUnderTolerance = %+.2w
  Inverted = false
  LineAngle = 0
  LockPosition = false
  MeasureType = 1
  OverTolerance = 0
  References2D = -> [View001]
  Rotation = 0
  ScaleType = 0
  TheoreticalExact = false
  Type = 1
  UnderTolerance = 0
  X = -19.8054
  Y = 28.6257
FEATURE [TechDraw::DrawViewDimension] Dimension015  label="Maß015"
  AngleOverride = false
  Arbitrary = false
  ArbitraryTolerances = false
  BoxCorners = (2) [(-69,-9.5,0),(69,9.5,0)]
  EqualTolerance = true
  ExtensionAngle = 0
  FormatSpec = %.2w
  FormatSpecOverTolerance = %+.2w
  FormatSpecUnderTolerance = %+.2w
  Inverted = false
  LineAngle = 0
  LockPosition = false
  MeasureType = 1
  OverTolerance = 0
  References2D = -> [View001]
  Rotation = 0
  ScaleType = 0
  TheoreticalExact = false
  Type = 1
  UnderTolerance = 0
  X = -62.5
  Y = 39.2313
FEATURE [TechDraw::DrawViewDimension] Dimension016  label="Maß016"
  AngleOverride = false
  Arbitrary = false
  ArbitraryTolerances = false
  BoxCorners = (2) [(-69,-9.5,0),(69,9.5,0)]
  EqualTolerance = true
  ExtensionAngle = 0
  FormatSpec = %.2w
  FormatSpecOverTolerance = %+.2w
  FormatSpecUnderTolerance = %+.2w
  Inverted = false
  LineAngle = 0
  LockPosition = false
  MeasureType = 1
  OverTolerance = 0
  References2D = -> [View001]
  Rotation = 0
  ScaleType = 0
  TheoreticalExact = false
  Type = 1
  UnderTolerance = 0
  X = 64.5
  Y = 35.6257
FEATURE [TechDraw::DrawViewDimension] Dimension017  label="Maß017"
  AngleOverride = false
  Arbitrary = false
  ArbitraryTolerances = false
  BoxCorners = (2) [(-8.5,-9.5,0),(8.5,9.5,0)]
  EqualTolerance = true
  ExtensionAngle = 0
  FormatSpec = %.2w
  FormatSpecOverTolerance = %+.2w
  FormatSpecUnderTolerance = %+.2w
  Inverted = false
  LineAngle = 0
  LockPosition = false
  MeasureType = 1
  OverTolerance = 0
  References2D = -> [ProjItem002]
  Rotation = 0
  ScaleType = 0
  TheoreticalExact = false
  Type = 1
  UnderTolerance = 0
  X = 0
  Y = 22.0971
FEATURE [TechDraw::DrawViewDimension] Dimension018  label="Maß018"
  AngleOverride = false
  Arbitrary = false
  ArbitraryTolerances = false
  BoxCorners = (2) [(-8.5,-9.5,0),(8.5,9.5,0)]
  EqualTolerance = true
  ExtensionAngle = 0
  FormatSpec = %.2w
  FormatSpecOverTolerance = %+.2w
  FormatSpecUnderTolerance = %+.2w
  Inverted = false
  LineAngle = 0
  LockPosition = false
  MeasureType = 1
  OverTolerance = 0
  References2D = -> [ProjItem002]
  Rotation = 0
  ScaleType = 0
  TheoreticalExact = false
  Type = 2
  UnderTolerance = 0
  X = 23.5578
  Y = 0
FEATURE [TechDraw::DrawViewDimension] Dimension019  label="Maß019"
  AngleOverride = false
  Arbitrary = false
  ArbitraryTolerances = false
  BoxCorners = (2) [(-8.5,-9.5,0),(8.5,9.5,0)]
  EqualTolerance = true
  ExtensionAngle = 0
  FormatSpec = %.2w
  FormatSpecOverTolerance = %+.2w
  FormatSpecUnderTolerance = %+.2w
  Inverted = false
  LineAngle = 0
  LockPosition = false
  MeasureType = 1
  OverTolerance = 0
  References2D = -> [ProjItem003]
  Rotation = 0
  ScaleType = 0
  TheoreticalExact = false
  Type = 1
  UnderTolerance = 0
  X = 0
  Y = 18.9747
FEATURE [TechDraw::DrawViewDimension] Dimension020  label="Maß020"
  AngleOverride = false
  Arbitrary = false
  ArbitraryTolerances = false
  BoxCorners = (2) [(-8.5,-9.5,0),(8.5,9.5,0)]
  EqualTolerance = true
  ExtensionAngle = 0
  FormatSpec = %.2w
  FormatSpecOverTolerance = %+.2w
  FormatSpecUnderTolerance = %+.2w
  Inverted = false
  LineAngle = 0
  LockPosition = false
  MeasureType = 1
  OverTolerance = 0
  References2D = -> [ProjItem003]
  Rotation = 0
  ScaleType = 0
  TheoreticalExact = false
  Type = 0
  UnderTolerance = 0
  X = -14.8332
  Y = 0
FEATURE [TechDraw::DrawViewDimension] Dimension021  label="Maß021"
  AngleOverride = false
  Arbitrary = false
  ArbitraryTolerances = false
  BoxCorners = (2) [(-8.5,-9.5,0),(8.5,9.5,0)]
  EqualTolerance = true
  ExtensionAngle = 0
  FormatSpec = %.2w
  FormatSpecOverTolerance = %+.2w
  FormatSpecUnderTolerance = %+.2w
  Inverted = false
  LineAngle = 0
  LockPosition = false
  MeasureType = 1
  OverTolerance = 0
  References2D = -> [ProjItem003]
  Rotation = 0
  ScaleType = 0
  TheoreticalExact = false
  Type = 1
  UnderTolerance = 0
  X = 0
  Y = 31.5767
FEATURE [TechDraw::DrawViewDimension] Dimension022  label="Maß022"
  AngleOverride = false
  Arbitrary = false
  ArbitraryTolerances = false
  BoxCorners = (2) [(-8.5,-9.5,0),(8.5,9.5,0)]
  EqualTolerance = true
  ExtensionAngle = 0
  FormatSpec = %.2w
  FormatSpecOverTolerance = %+.2w
  FormatSpecUnderTolerance = %+.2w
  Inverted = false
  LineAngle = 0
  LockPosition = false
  MeasureType = 1
  OverTolerance = 0
  References2D = -> [ProjItem003]
  Rotation = 0
  ScaleType = 0
  TheoreticalExact = false
  Type = 2
  UnderTolerance = 0
  X = 14.9712
  Y = 0
FEATURE [TechDraw::DrawViewDimension] Dimension023  label="Maß023"
  AngleOverride = false
  Arbitrary = false
  ArbitraryTolerances = false
  BoxCorners = (2) [(-69,-9.5,0),(69,9.5,0)]
  EqualTolerance = true
  ExtensionAngle = 0
  FormatSpec = %.2w
  FormatSpecOverTolerance = %+.2w
  FormatSpecUnderTolerance = %+.2w
  Inverted = false
  LineAngle = 0
  LockPosition = false
  MeasureType = 1
  OverTolerance = 0
  References2D = -> [View001]
  Rotation = 0
  ScaleType = 0
  TheoreticalExact = false
  Type = 1
  UnderTolerance = 0
  X = 33.2248
  Y = -35.5341
FEATURE [TechDraw::DrawPage] Page  label="TX Axle"
  KeepUpdated = true
  NextBalloonIndex = 1
  ProjectionType = 0
  Template = -> Template
  Views = -> [ProjGroup001,Dimension014,Dimension015,Dimension016,Dimension017,Dimension018,Dimension019,Dimension020,Dimension021,Dimension022,Dimension023]
note: 2 file-system paths scrubbed to <path> (originals preserved in the JSON sidecar)
